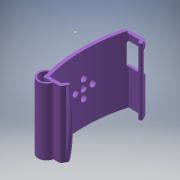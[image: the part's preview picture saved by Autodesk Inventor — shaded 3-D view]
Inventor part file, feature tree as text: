
AUTODESK INVENTOR PART (.ipt)
format: ipt  version: 2016 (Build 200138000, 138)  size: 505,344 bytes
history: native  units: mm
features: sketch x11, extrude x8, fillet x4, hole x3, projected_geometry x3, plane x2, pattern_circular x2, other x1
ambient origin geometry x8: Origin, YZ Plane, XZ Plane, XY Plane, X Axis, Y Axis, Z Axis, Center Point
bodies: Body1 (feature_tree)
feature tree (34):
  extrude  "Extrusion2"  Depth=3.0mm
  plane  "Work Plane1"
  extrude  "Extrusion4"  Depth=3.0mm
  fillet  "Fillet1"  Radius=80.0mm
  extrude  "Extrusion6"  Depth=5.0mm TaperAngle=0.0deg
  extrude  "Extrusion7"  Depth=10.0mm TaperAngle=0.0deg
  fillet  "Fillet2"  Radius=10.0mm
  extrude  "Extrusion8"  Depth=10.0mm
  fillet  "Fillet3"  Radius=10.0mm
  extrude  "Extrusion9"  Depth=1.5mm
  fillet  "Fillet4"  Radius=20.0mm
  extrude  "Extrusion10"  Depth=10.0mm TaperAngle=0.0deg
  sketch  "Sketch15"  dims[d45=1.5mm d46=0.0mm d47=0.0mm]
  sketch  "Sketch19"  dims[d103=-3.499993mm d124=5.7658mm d125=19.05mm d126=5.7912mm d127=3.5306mm d128=14.3117mm d129=15.859519mm d130=20.594885mm d160=7.7724mm]
  plane  "Work Plane2"
  hole  "Hole1"  [1 undecoded]
  hole  "Hole4"  [1 undecoded]
  pattern_circular  "Circular Pattern2"  Count=4 Angle=360.0deg
  hole  "Hole6"  [1 undecoded]
  extrude  "Extrusion18"  Depth=25.4mm TaperAngle=0.0deg
  pattern_circular  "Circular Pattern3"  [2 undecoded]
  sketch  "Sketch1"  dims[d5=3.0mm d6=3.0mm]
  other  "Work Axis1"
  sketch  "Sketch6"  dims[d7=3.0mm d11=3.0mm d13=80.0mm d14=0.0mm]
  sketch  "Sketch8"  dims[d18=28.5mm d19=5.0mm d20=0.0mm]
  projected_geometry  "Projected Loop1"
  sketch  "Sketch9"  dims[d21=2.5mm d22=0.0mm d27=2.0mm d31=10.0mm d32=0.0mm d33=10.0mm d34=0.0mm]
  projected_geometry  "Projected Loop2"
  sketch  "Sketch10"  dims[d35=3.0mm d36=2.0mm d37=10.0mm d38=0.0mm]
  projected_geometry  "Projected Loop3"
  sketch  "Sketch11"  dims[d39=1.5mm d40=30.0mm d41=20.0mm]
  sketch  "Sketch12"  dims[d42=2.0mm d43=10.0mm d44=0.0mm]
  sketch  "Sketch28"  dims[d161=5.7404mm d162=19.05mm d163=5.7658mm d164=3.5052mm d165=14.3117mm d166=15.859519mm d167=20.594885mm d168=40.0mm d169=360.0deg]
  sketch  "Sketch29"  dims[d180=25.4mm d181=25.4mm d182=3.5306mm d183=19.05mm d184=5.7658mm d185=3.5052mm d186=14.3117mm d187=15.859519mm d188=20.594885mm d189=40.0mm d190=360.0deg d192=25.4mm d193=0.0mm d196=71.374mm d171=25.4mm d172=25.4mm]
note: 5 required parameter values undecoded (feature->parameter linkage not recoverable at this tier; creation-order binding heuristic only, values carry confidence <= 0.55)
